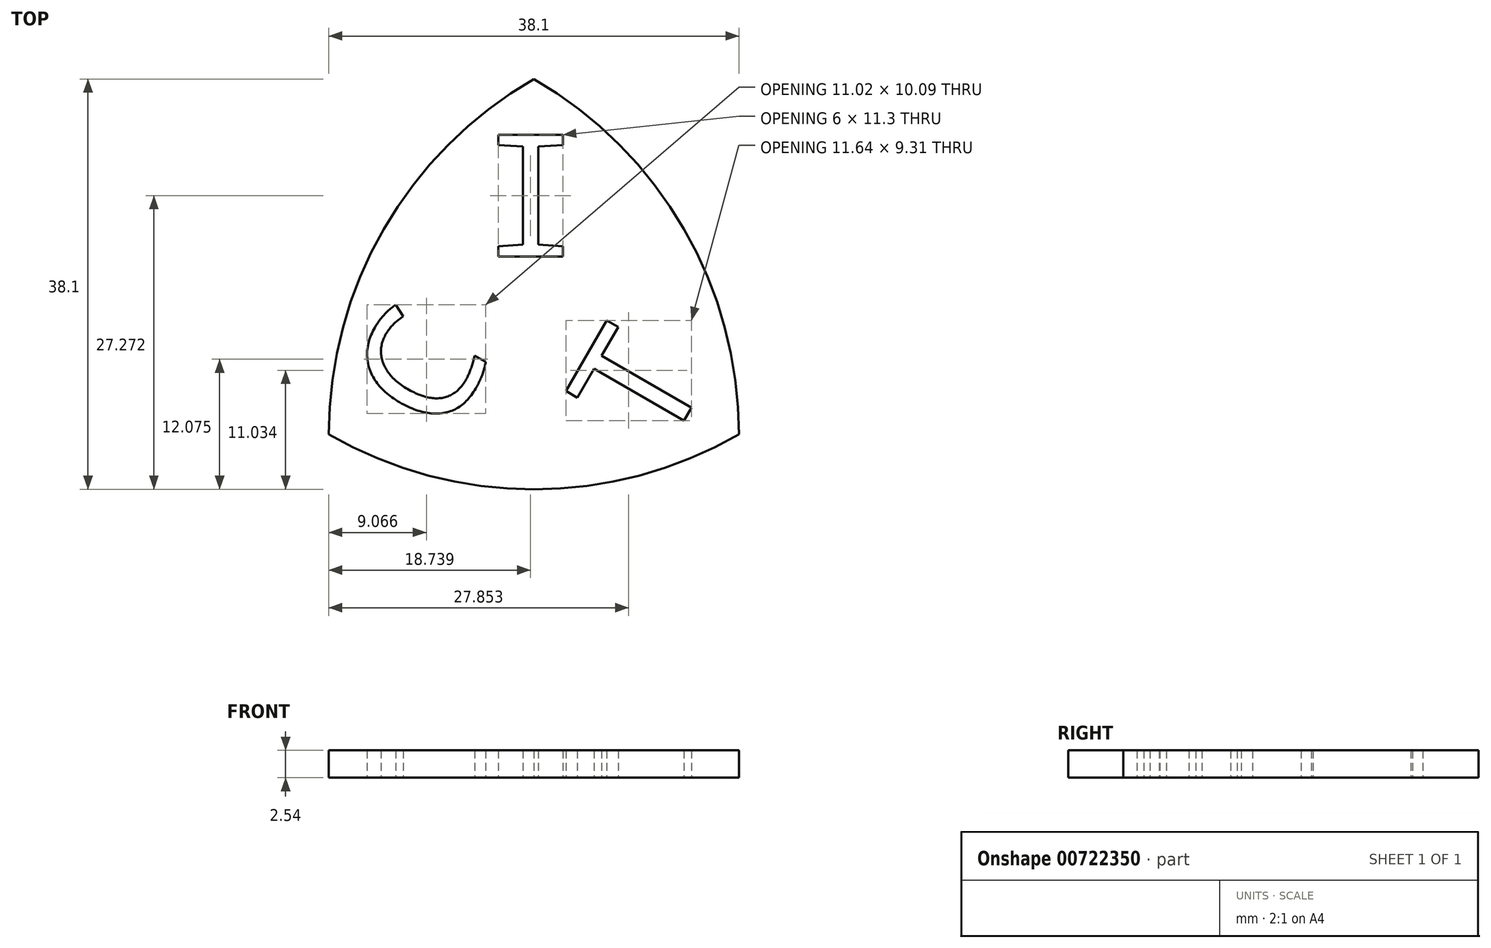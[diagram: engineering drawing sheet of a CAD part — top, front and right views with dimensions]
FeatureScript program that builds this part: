
annotation { "Feature Type Name" : "Feature", "Feature Type Description" : "" }
export const myFeature = defineFeature(function(context is Context, id is Id, definition is map)
    precondition{}
    {
        {
            var Q0;
            Q0=qCreatedBy(makeId("Top.planeOp"),FACE);
            var sketch = newSketch(context, id + "F0", { "sketchPlane" : qUnion([Q0])});
            skCircle(sketch, "E0", {"center": v(0, 0) * mm, "radius": 38.1 * mm});
            skSolve(sketch);
        }
        {
            var Q0;
            Q0=qCreatedBy(makeId("Top.planeOp"),FACE);
            var sketch = newSketch(context, id + "F1", { "sketchPlane" : qUnion([Q0])});
            skCircle(sketch, "E1", {"center": v(-38.1, 0) * mm, "radius": 38.1 * mm});
            skSolve(sketch);
        }
        {
            var Q0;
            Q0=qCreatedBy(makeId("Top.planeOp"),FACE);
            var sketch = newSketch(context, id + "F2", { "sketchPlane" : qUnion([Q0])});
            skCircle(sketch, "E2", {"center": v(-19.05, 33) * mm, "radius": 38.1 * mm});
            skSolve(sketch);
        }
        {
            var Q0;
            Q0 = qSketchRegion(id + "F0", true);
            extrude(context, id + "F3", {"entities" : qUnion([Q0]), "depth" : 2.54 * mm, "offsetDistance" : 25.4 * mm});
        }
        {
            var Q0;
            Q0 = qSketchRegion(id + "F1", true);
            extrude(context, id + "F4", {"entities" : qUnion([Q0]), "depth" : 2.54 * mm, "offsetDistance" : 25.4 * mm});
        }
        {
            var Q0;
            Q0 = qSketchRegion(id + "F2", true);
            extrude(context, id + "F5", {"entities" : qUnion([Q0]), "depth" : 2.54 * mm, "offsetDistance" : 25.4 * mm});
        }
        {
            var Q0;
            Q0=makeQuery(id+"F3.opExtrude","SWEPT_BODY",BODY,{"disambiguationData":[OSD([sQuery(id+"F0.wireOp",EDGE,"E0")])]});
            var Q1;
            Q1=makeQuery(id+"F4.opExtrude","SWEPT_BODY",BODY,{"disambiguationData":[OSD([sQuery(id+"F1.wireOp",EDGE,"E1")])]});
            var Q2;
            Q2=makeQuery(id+"F5.opExtrude","SWEPT_BODY",BODY,{"disambiguationData":[OSD([sQuery(id+"F2.wireOp",EDGE,"E2")])]});
            booleanBodies(context, id + "F6", {"operationType" : BooleanOperationType.INTERSECTION, "tools" : qUnion([Q0, Q1, Q2])});
        }
        {
            var Q0;
            Q0=qCreatedBy(makeId("Top.planeOp"),FACE);
            var sketch = newSketch(context, id + "F7", { "sketchPlane" : qUnion([Q0])});
            skText(sketch, "E3", { "text": "C", "fontName": "DroidSansMono.ttf"});
            const initialGuessF7  = {"E3": [-0.02737, -0.0005, 0.5, 0.86603, 0.01073]};
            skSetInitialGuess(sketch, initialGuessF7);
            skSolve(sketch);
        }
        {
            var Q0;
            Q0=qCreatedBy(makeId("Top.planeOp"),FACE);
            var sketch = newSketch(context, id + "F8", { "sketchPlane" : qUnion([Q0])});
            skText(sketch, "E4", { "text": "I", "fontName": "DroidSansMono.ttf"});
            const initialGuessF8  = {"E4": [-0.0241, 0.01652, 1, 0, 0.0114]};
            skSetInitialGuess(sketch, initialGuessF8);
            skSolve(sketch);
        }
        {
            var Q0;
            Q0=qCreatedBy(makeId("Top.planeOp"),FACE);
            var sketch = newSketch(context, id + "F9", { "sketchPlane" : qUnion([Q0])});
            skText(sketch, "E5", { "text": "T", "fontName": "DroidSansMono.ttf"});
            const initialGuessF9  = {"E5": [-0.00705, -0.00206, 0.5, 0.86603, 0.01094]};
            skSetInitialGuess(sketch, initialGuessF9);
            skSolve(sketch);
        }
        {
            var Q0;
            Q0 = qSketchRegion(id + "F7", true);
            var Q1;
            Q1 = qSketchRegion(id + "F8", true);
            var Q2;
            Q2 = qSketchRegion(id + "F9", true);
            extrude(context, id + "F10", {"entities" : qUnion([Q0, Q1, Q2]), "depth" : 2.54 * mm, "offsetDistance" : 25.4 * mm});
        }
        {
            var Q0;
            Q0=makeQuery(id+"F10.opExtrude","SWEPT_BODY",BODY,{"disambiguationData":[OSD([sQuery(id+"F7.wireOp",EDGE,"E3.sketch_text.stroke-0"),sQuery(id+"F7.wireOp",EDGE,"E3.sketch_text.stroke-1"),sQuery(id+"F7.wireOp",EDGE,"E3.sketch_text.stroke-2"),sQuery(id+"F7.wireOp",EDGE,"E3.sketch_text.stroke-3"),sQuery(id+"F7.wireOp",EDGE,"E3.sketch_text.stroke-4"),sQuery(id+"F7.wireOp",EDGE,"E3.sketch_text.stroke-5"),sQuery(id+"F7.wireOp",EDGE,"E3.sketch_text.stroke-6"),sQuery(id+"F7.wireOp",EDGE,"E3.sketch_text.stroke-7"),sQuery(id+"F7.wireOp",EDGE,"E3.sketch_text.stroke-8"),sQuery(id+"F7.wireOp",EDGE,"E3.sketch_text.stroke-9"),sQuery(id+"F7.wireOp",EDGE,"E3.sketch_text.stroke-10"),sQuery(id+"F7.wireOp",EDGE,"E3.sketch_text.stroke-11"),sQuery(id+"F7.wireOp",EDGE,"E3.sketch_text.stroke-12"),sQuery(id+"F7.wireOp",EDGE,"E3.sketch_text.stroke-13")])]});
            var Q1;
            Q1=makeQuery(id+"F10.opExtrude","SWEPT_BODY",BODY,{"disambiguationData":[OSD([sQuery(id+"F8.wireOp",EDGE,"E4.sketch_text.stroke-0"),sQuery(id+"F8.wireOp",EDGE,"E4.sketch_text.stroke-1"),sQuery(id+"F8.wireOp",EDGE,"E4.sketch_text.stroke-2"),sQuery(id+"F8.wireOp",EDGE,"E4.sketch_text.stroke-3"),sQuery(id+"F8.wireOp",EDGE,"E4.sketch_text.stroke-4"),sQuery(id+"F8.wireOp",EDGE,"E4.sketch_text.stroke-5"),sQuery(id+"F8.wireOp",EDGE,"E4.sketch_text.stroke-6"),sQuery(id+"F8.wireOp",EDGE,"E4.sketch_text.stroke-7"),sQuery(id+"F8.wireOp",EDGE,"E4.sketch_text.stroke-8"),sQuery(id+"F8.wireOp",EDGE,"E4.sketch_text.stroke-9"),sQuery(id+"F8.wireOp",EDGE,"E4.sketch_text.stroke-10"),sQuery(id+"F8.wireOp",EDGE,"E4.sketch_text.stroke-11")])]});
            var Q2;
            Q2=makeQuery(id+"F10.opExtrude","SWEPT_BODY",BODY,{"disambiguationData":[OSD([sQuery(id+"F9.wireOp",EDGE,"E5.sketch_text.stroke-0"),sQuery(id+"F9.wireOp",EDGE,"E5.sketch_text.stroke-1"),sQuery(id+"F9.wireOp",EDGE,"E5.sketch_text.stroke-2"),sQuery(id+"F9.wireOp",EDGE,"E5.sketch_text.stroke-3"),sQuery(id+"F9.wireOp",EDGE,"E5.sketch_text.stroke-4"),sQuery(id+"F9.wireOp",EDGE,"E5.sketch_text.stroke-5"),sQuery(id+"F9.wireOp",EDGE,"E5.sketch_text.stroke-6"),sQuery(id+"F9.wireOp",EDGE,"E5.sketch_text.stroke-7")])]});
            var Q3;
            Q3=makeQuery(id+"F6.opBoolean","INTERSECT",BODY,{"derivedFrom":[makeQuery(id+"F3.opExtrude","SWEPT_BODY",BODY,{"disambiguationData":[OSD([sQuery(id+"F0.wireOp",EDGE,"E0")])]}),makeQuery(id+"F4.opExtrude","SWEPT_BODY",BODY,{"disambiguationData":[OSD([sQuery(id+"F1.wireOp",EDGE,"E1")])]}),makeQuery(id+"F5.opExtrude","SWEPT_BODY",BODY,{"disambiguationData":[OSD([sQuery(id+"F2.wireOp",EDGE,"E2")])]})]});
            booleanBodies(context, id + "F11", {"operationType" : BooleanOperationType.SUBTRACTION, "tools" : qUnion([Q0, Q1, Q2]), "targets" : qUnion([Q3])});
        }
    });
